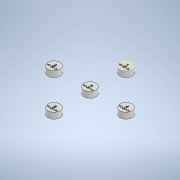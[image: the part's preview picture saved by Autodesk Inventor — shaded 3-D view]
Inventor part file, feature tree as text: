
AUTODESK INVENTOR PART (.ipt)
format: ipt  version: 2020.3 (Build 243373000, 373)  size: 414,208 bytes
history: native  units: in
note: dims shown in document units (in); Inventor stores cm internally (conversion verified against a paired STEP export)
features: sketch x3, extrude x2
ambient origin geometry x8: Origin, YZ Plane, XZ Plane, XY Plane, X Axis, Y Axis, Z Axis, Center Point
bodies: Solid1 (feature_tree)
feature tree (5):
  extrude  "Extrusion1"  Depth=3.0in
  sketch  "Sketch4"  dims[d2=3.0in d3=3.0in]
  extrude  "Extrusion4"  Depth=3.0in
  sketch  "Sketch1"  dims[d0=1.0in d1=3.0in]
  sketch  "Sketch5"  dims[d4=3.0in d5=0.5in d6=0.0in d11=0.2in d12=0.0in]
